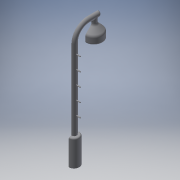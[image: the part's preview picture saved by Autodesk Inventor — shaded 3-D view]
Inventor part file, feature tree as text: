
AUTODESK INVENTOR PART (.ipt)
format: ipt  version: 2018 (Build 220112000, 112)  size: 301,056 bytes
history: native  units: in
note: dims shown in document units (in); Inventor stores cm internally (conversion verified against a paired STEP export)
features: other x3, sketch x2
ambient origin geometry x8: Origin, YZ Plane, XZ Plane, XY Plane, X Axis, Y Axis, Z Axis, Center Point
bodies: Solid1 (feature_tree)
feature tree (5):
  other  "lampa_nadrazni.ipt"
  other  "Solid1::lampa_nadrazni.ipt"
  other  "TaggingFeature1"
  sketch  "Sketch1"  dims[d0=0.3937in]
  sketch  "Sketch11"
